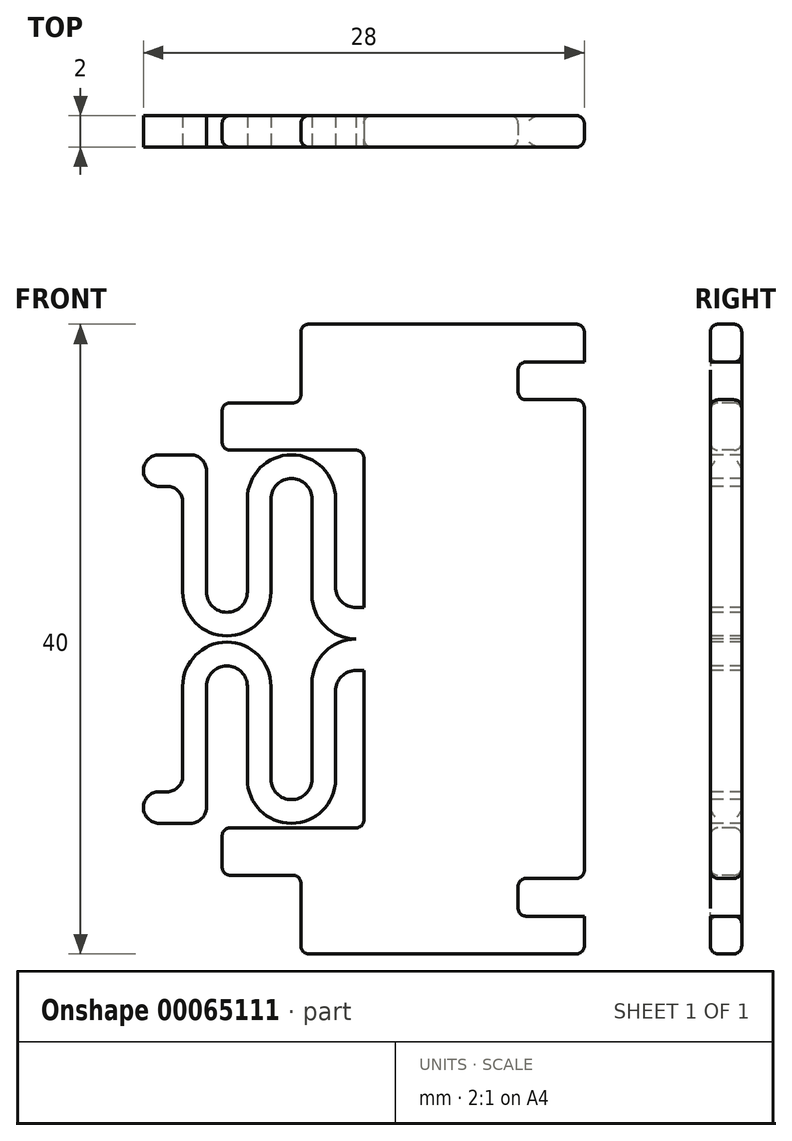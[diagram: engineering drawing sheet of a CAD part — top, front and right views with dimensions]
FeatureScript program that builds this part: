
annotation { "Feature Type Name" : "Feature", "Feature Type Description" : "" }
export const myFeature = defineFeature(function(context is Context, id is Id, definition is map)
    precondition{}
    {
        {
            var Q0;
            Q0=qCreatedBy(makeId("Top.planeOp"),FACE);
            var sketch = newSketch(context, id + "F0", { "sketchPlane" : qUnion([Q0])});
            skLineSegment(sketch, "E0.bottom", {"start": v(0, 0) * mm, "end": v(-18, 0) * mm});
            skLineSegment(sketch, "E0.top", {"start": v(0, 2) * mm, "end": v(-18, 2) * mm});
            skLineSegment(sketch, "E0.left", {"start": v(0, 0) * mm, "end": v(0, 2) * mm});
            skLineSegment(sketch, "E0.right", {"start": v(-18, 0) * mm, "end": v(-18, 2) * mm});
            skSolve(sketch);
        }
        {
            var Q0;
            Q0 = qSketchRegion(id + "F0", true);
            extrude(context, id + "F1", {"entities" : qUnion([Q0]), "depth" : 20 * mm});
        }
        {
            var Q0;
            Q0=qCreatedBy(makeId("Front.planeOp"),FACE);
            var sketch = newSketch(context, id + "F2", { "sketchPlane" : qUnion([Q0])});
            skLineSegment(sketch, "E1.bottom", {"start": v(-4.2, 17.6) * mm, "end": v(0, 17.6) * mm});
            skLineSegment(sketch, "E1.top", {"start": v(-4.2, 15.2) * mm, "end": v(0, 15.2) * mm});
            skLineSegment(sketch, "E1.left", {"start": v(-4.2, 17.6) * mm, "end": v(-4.2, 15.2) * mm});
            skLineSegment(sketch, "E1.right", {"start": v(0, 17.6) * mm, "end": v(0, 15.2) * mm});
            skSolve(sketch);
        }
        {
            var Q0;
            Q0 = qSketchRegion(id + "F2", true);
            extrude(context, id + "F3", {"entities" : qUnion([Q0]), "operationType" : NewBodyOperationType.REMOVE, "endBound" : BoundingType.THROUGH_ALL, "oppositeDirection" : true, "depth" : 25 * mm});
        }
        {
            var Q0;
            Q0=qCreatedBy(makeId("Front.planeOp"),FACE);
            var sketch = newSketch(context, id + "F4", { "sketchPlane" : qUnion([Q0])});
            skLineSegment(sketch, "E2.bottom", {"start": v(-14, 12) * mm, "end": v(-18, 12) * mm});
            skLineSegment(sketch, "E2.top", {"start": v(-14, 0) * mm, "end": v(-18, 0) * mm});
            skLineSegment(sketch, "E2.left", {"start": v(-14, 12) * mm, "end": v(-14, 0) * mm});
            skLineSegment(sketch, "E2.right", {"start": v(-18, 12) * mm, "end": v(-18, 0) * mm});
            skSolve(sketch);
        }
        {
            var Q0;
            Q0 = qSketchRegion(id + "F4", true);
            extrude(context, id + "F5", {"entities" : qUnion([Q0]), "operationType" : NewBodyOperationType.REMOVE, "endBound" : BoundingType.THROUGH_ALL, "oppositeDirection" : true, "depth" : 25 * mm});
        }
        {
            var Q0;
            Q0=qCreatedBy(makeId("Front.planeOp"),FACE);
            var sketch = newSketch(context, id + "F6", { "sketchPlane" : qUnion([Q0])});
            skLineSegment(sketch, "E3", {"start": v(-15.8, 11.7) * mm, "end": v(-21.4, 11.7) * mm, "construction": true});
            skLineSegment(sketch, "E4", {"start": v(-21.4, 11.7) * mm, "end": v(-21.4, 8.9) * mm, "construction": true});
            skLineSegment(sketch, "E5", {"start": v(-21.4, 1.7) * mm, "end": v(-24, 1.7) * mm, "construction": true});
            skLineSegment(sketch, "E6", {"start": v(-24, 1.7) * mm, "end": v(-24, 3) * mm, "construction": true});
            skLineSegment(sketch, "E7", {"start": v(-24, 11.7) * mm, "end": v(-28, 11.7) * mm});
            skLineSegment(sketch, "E8", {"start": v(-28, 11.7) * mm, "end": v(-28, 9.7) * mm});
            skLineSegment(sketch, "E9", {"start": v(-28, 9.7) * mm, "end": v(-25.5, 9.7) * mm});
            skLineSegment(sketch, "E10", {"start": v(-25.5, 9.7) * mm, "end": v(-25.5, 3) * mm});
            skLineSegment(sketch, "E11", {"start": v(-25.5, 0.2) * mm, "end": v(-19.9, 0.2) * mm, "construction": true});
            skLineSegment(sketch, "E12", {"start": v(-19.9, 0.2) * mm, "end": v(-19.9, 3) * mm, "construction": true});
            skLineSegment(sketch, "E13", {"start": v(-19.9, 10.2) * mm, "end": v(-17.3, 10.2) * mm, "construction": true});
            skLineSegment(sketch, "E14.bottom", {"start": v(-23, 15) * mm, "end": v(-18, 15) * mm});
            skLineSegment(sketch, "E14.top", {"start": v(-23, 12) * mm, "end": v(-18, 12) * mm});
            skLineSegment(sketch, "E14.left", {"start": v(-23, 15) * mm, "end": v(-23, 12) * mm});
            skLineSegment(sketch, "E14.right", {"start": v(-18, 15) * mm, "end": v(-18, 12) * mm});
            skArc(sketch, "E15", {"start": v(-24, 3) * mm, "mid": v(-22.7, 1.7) * mm, "end": v(-21.4, 3) * mm});
            skArc(sketch, "E16", {"start": v(-25.5, 3) * mm, "mid": v(-22.7, 0.2) * mm, "end": v(-19.9, 3) * mm});
            skLineSegment(sketch, "E17", {"start": v(-24, 3) * mm, "end": v(-24, 11.7) * mm});
            skLineSegment(sketch, "E18", {"start": v(-25.5, 3) * mm, "end": v(-25.5, 0.2) * mm, "construction": true});
            skLineSegment(sketch, "E19", {"start": v(-21.4, 3) * mm, "end": v(-21.4, 1.7) * mm, "construction": true});
            skLineSegment(sketch, "E20", {"start": v(-19.9, 3) * mm, "end": v(-19.9, 8.9) * mm});
            skArc(sketch, "E21", {"start": v(-15.8, 8.9) * mm, "mid": v(-18.6, 11.7) * mm, "end": v(-21.4, 8.9) * mm});
            skArc(sketch, "E22", {"start": v(-17.3, 8.9) * mm, "mid": v(-18.6, 10.2) * mm, "end": v(-19.9, 8.9) * mm});
            skLineSegment(sketch, "E23", {"start": v(-17.3, 10.2) * mm, "end": v(-17.3, 8.9) * mm, "construction": true});
            skLineSegment(sketch, "E24", {"start": v(-14.5, 0) * mm, "end": v(-14, 0) * mm});
            skLineSegment(sketch, "E25", {"start": v(-14, 0) * mm, "end": v(-14, 2) * mm});
            skLineSegment(sketch, "E26", {"start": v(-14, 2) * mm, "end": v(-14.5, 2) * mm});
            skLineSegment(sketch, "E27", {"start": v(-15.8, 3.3) * mm, "end": v(-15.8, 8.9) * mm});
            skLineSegment(sketch, "E28", {"start": v(-17.3, 8.9) * mm, "end": v(-17.3, 2.8) * mm});
            skLineSegment(sketch, "E29", {"start": v(-19.9, 8.9) * mm, "end": v(-19.9, 10.2) * mm, "construction": true});
            skLineSegment(sketch, "E30", {"start": v(-21.4, 8.9) * mm, "end": v(-21.4, 3) * mm});
            skLineSegment(sketch, "E31", {"start": v(-15.8, 8.9) * mm, "end": v(-15.8, 11.7) * mm, "construction": true});
            skPoint(sketch, "E32.visualSharp", {"position": v(-15.8, 2) * mm});
            skArc(sketch, "E32.filletArc", {"start": v(-15.8, 3.3) * mm, "mid": v(-15.42, 2.38) * mm, "end": v(-14.5, 2) * mm});
            skPoint(sketch, "E33.visualSharp", {"position": v(-17.3, 0) * mm});
            skArc(sketch, "E33.filletArc", {"start": v(-17.3, 2.8) * mm, "mid": v(-16.48, 0.82) * mm, "end": v(-14.5, 0) * mm});
            skSolve(sketch);
        }
        {
            var Q0;
            Q0 = qSketchRegion(id + "F6", true);
            extrude(context, id + "F7", {"entities" : qUnion([Q0]), "operationType" : NewBodyOperationType.ADD, "oppositeDirection" : true, "depth" : 2 * mm});
        }
        {
            var Q0;
            Q0=makeQuery(id+"F7.opExtrude","SWEPT_EDGE",EDGE,{"disambiguationData":[OSD([sQuery(id+"F6.wireOp",EDGE,"E6"),sQuery(id+"F6.wireOp",EDGE,"E7")])]});
            var Q1;
            Q1=makeQuery(id+"F7.opExtrude","SWEPT_EDGE",EDGE,{"disambiguationData":[OSD([sQuery(id+"F6.wireOp",EDGE,"E11"),sQuery(id+"F6.wireOp",EDGE,"E12")])]});
            var Q2;
            Q2=makeQuery(id+"F7.opExtrude","SWEPT_EDGE",EDGE,{"disambiguationData":[OSD([sQuery(id+"F6.wireOp",EDGE,"E10"),sQuery(id+"F6.wireOp",EDGE,"E11")])]});
            var Q3;
            Q3=makeQuery(id+"F7.opExtrude","SWEPT_EDGE",EDGE,{"disambiguationData":[OSD([sQuery(id+"F6.wireOp",EDGE,"E7"),sQuery(id+"F6.wireOp",EDGE,"E8")])]});
            var Q4;
            Q4=makeQuery(id+"F7.opExtrude","SWEPT_EDGE",EDGE,{"disambiguationData":[OSD([sQuery(id+"F6.wireOp",EDGE,"E8"),sQuery(id+"F6.wireOp",EDGE,"E9")])]});
            var Q5;
            Q5=makeQuery(id+"F7.opExtrude","SWEPT_EDGE",EDGE,{"disambiguationData":[OSD([sQuery(id+"F6.wireOp",EDGE,"E3"),sQuery(id+"F6.wireOp",EDGE,"E4")])]});
            var Q6;
            Q6=makeQuery(id+"F7.opExtrude","SWEPT_EDGE",EDGE,{"disambiguationData":[OSD([sQuery(id+"F6.wireOp",EDGE,"E25"),sQuery(id+"F6.wireOp",EDGE,"E26")])]});
            fillet(context, id + "F8", {"entities" : qUnion([Q0, Q1, Q2, Q3, Q4, Q5, Q6]), "radius" : 1 * mm, "tangentPropagation" : true, "allowEdgeOverflow" : false});
        }
        {
            var Q0;
            Q0=makeQuery(id+"F1.opExtrude","CAP_FACE",FACE,{"disambiguationData":[OSD([sQuery(id+"F0.wireOp",EDGE,"E0.bottom"),sQuery(id+"F0.wireOp",EDGE,"E0.top"),sQuery(id+"F0.wireOp",EDGE,"E0.left"),sQuery(id+"F0.wireOp",EDGE,"E0.right")])],"isStart":false});
            var Q1;
            {var subQ0=sQuery(id+"F0.wireOp",EDGE,"E0.bottom");var subQ1=sQuery(id+"F0.wireOp",EDGE,"E0.left");Q1=makeQuery(id+"F3.boolean.opBoolean","SPLIT",EDGE,{"disambiguationData":[TD([makeQuery(id+"F3.opExtrude","SWEPT_FACE",FACE,{"disambiguationData":[OSD([sQuery(id+"F2.wireOp",EDGE,"E1.bottom")])]})])],"derivedFrom":makeQuery(id+"F1.opExtrude","SWEPT_EDGE",EDGE,{"disambiguationData":[OSD([subQ0,subQ1])]})});}
            var Q2;
            {var subQ0=sQuery(id+"F0.wireOp",EDGE,"E0.bottom");var subQ1=sQuery(id+"F0.wireOp",EDGE,"E0.left");Q2=makeQuery(id+"F3.boolean.opBoolean","SPLIT",EDGE,{"disambiguationData":[TD([makeQuery(id+"F3.opExtrude","SWEPT_FACE",FACE,{"disambiguationData":[OSD([sQuery(id+"F2.wireOp",EDGE,"E1.top")])]})])],"derivedFrom":makeQuery(id+"F1.opExtrude","SWEPT_EDGE",EDGE,{"disambiguationData":[OSD([subQ0,subQ1])]})});}
            var Q3;
            {var subQ0=sQuery(id+"F0.wireOp",EDGE,"E0.left");var subQ1=sQuery(id+"F0.wireOp",EDGE,"E0.top");Q3=makeQuery(id+"F3.boolean.opBoolean","SPLIT",EDGE,{"disambiguationData":[TD([makeQuery(id+"F3.opExtrude","SWEPT_FACE",FACE,{"disambiguationData":[OSD([sQuery(id+"F2.wireOp",EDGE,"E1.top")])]})])],"derivedFrom":makeQuery(id+"F1.opExtrude","SWEPT_EDGE",EDGE,{"disambiguationData":[OSD([subQ1,subQ0])]})});}
            var Q4;
            {var subQ0=sQuery(id+"F0.wireOp",EDGE,"E0.left");var subQ1=sQuery(id+"F0.wireOp",EDGE,"E0.top");Q4=makeQuery(id+"F3.boolean.opBoolean","SPLIT",EDGE,{"disambiguationData":[TD([makeQuery(id+"F3.opExtrude","SWEPT_FACE",FACE,{"disambiguationData":[OSD([sQuery(id+"F2.wireOp",EDGE,"E1.bottom")])]})])],"derivedFrom":makeQuery(id+"F1.opExtrude","SWEPT_EDGE",EDGE,{"disambiguationData":[OSD([subQ1,subQ0])]})});}
            var Q5;
            Q5=makeQuery(id+"F3.boolean.opBoolean","COPY",EDGE,{"derivedFrom":makeQuery(id+"F3.opExtrude","SWEPT_EDGE",EDGE,{"disambiguationData":[OSD([sQuery(id+"F2.wireOp",EDGE,"E1.bottom"),sQuery(id+"F2.wireOp",EDGE,"E1.right")])]})});
            var Q6;
            Q6=makeQuery(id+"F3.boolean.opBoolean","COPY",FACE,{"derivedFrom":makeQuery(id+"F3.opExtrude","SWEPT_FACE",FACE,{"disambiguationData":[OSD([sQuery(id+"F2.wireOp",EDGE,"E1.left")])]})});
            var Q7;
            Q7=makeQuery(id+"F3.boolean.opBoolean","COPY",EDGE,{"derivedFrom":makeQuery(id+"F3.opExtrude","SWEPT_EDGE",EDGE,{"disambiguationData":[OSD([sQuery(id+"F2.wireOp",EDGE,"E1.bottom"),sQuery(id+"F2.wireOp",EDGE,"E1.left")])]})});
            var Q8;
            Q8=makeQuery(id+"F3.boolean.opBoolean","COPY",FACE,{"derivedFrom":makeQuery(id+"F3.opExtrude","SWEPT_FACE",FACE,{"disambiguationData":[OSD([sQuery(id+"F2.wireOp",EDGE,"E1.top")])]})});
            var Q9;
            Q9=makeQuery(id+"F7.opExtrude","SWEPT_FACE",FACE,{"disambiguationData":[OSD([sQuery(id+"F6.wireOp",EDGE,"E14.top")])]});
            var Q10;
            Q10=makeQuery(id+"F7.opExtrude","SWEPT_FACE",FACE,{"disambiguationData":[OSD([sQuery(id+"F6.wireOp",EDGE,"E14.left")])]});
            var Q11;
            {var subQ15=sQuery(id+"F6.wireOp",EDGE,"E14.bottom");var subQ17=sQuery(id+"F0.wireOp",EDGE,"E0.right");Q11=makeQuery(id+"F7.boolean.opBoolean","SPLIT",FACE,{"disambiguationData":[TD([makeQuery(id+"F7.opExtrude","SWEPT_FACE",FACE,{"disambiguationData":[OSD([subQ15])]})])],"derivedFrom":makeQuery(id+"F1.opExtrude","SWEPT_FACE",FACE,{"disambiguationData":[OSD([subQ17])]})});}
            var Q12;
            Q12=makeQuery(id+"F7.opExtrude","SWEPT_FACE",FACE,{"disambiguationData":[OSD([sQuery(id+"F6.wireOp",EDGE,"E14.bottom")])]});
            var Q13;
            {var subQ0=sQuery(id+"F6.wireOp",EDGE,"E13");var subQ1=sQuery(id+"F0.wireOp",EDGE,"E0.right");var subQ2=sQuery(id+"F0.wireOp",EDGE,"E0.bottom");Q13=makeQuery(id+"F7.boolean.opBoolean","SPLIT",EDGE,{"disambiguationData":[TD([makeQuery(id+"F7.opExtrude","SWEPT_FACE",FACE,{"disambiguationData":[OSD([subQ0])]})])],"derivedFrom":makeQuery(id+"F1.opExtrude","SWEPT_EDGE",EDGE,{"disambiguationData":[OSD([subQ2,subQ1])]})});}
            var Q14;
            {var subQ0=sQuery(id+"F0.wireOp",EDGE,"E0.right");var subQ1=sQuery(id+"F6.wireOp",EDGE,"E13");var subQ2=sQuery(id+"F0.wireOp",EDGE,"E0.top");Q14=makeQuery(id+"F7.boolean.opBoolean","SPLIT",EDGE,{"disambiguationData":[TD([makeQuery(id+"F7.opExtrude","SWEPT_FACE",FACE,{"disambiguationData":[OSD([subQ1])]})])],"derivedFrom":makeQuery(id+"F1.opExtrude","SWEPT_EDGE",EDGE,{"disambiguationData":[OSD([subQ2,subQ0])]})});}
            fillet(context, id + "F9", {"entities" : qUnion([Q0, Q1, Q2, Q3, Q4, Q5, Q6, Q7, Q8, Q9, Q10, Q11, Q12, Q13, Q14]), "radius" : .5 * mm, "tangentPropagation" : true, "allowEdgeOverflow" : false});
        }
        {
            var Q0;
            Q0=makeQuery(id+"F1.opExtrude","SWEPT_BODY",BODY,{"disambiguationData":[OSD([sQuery(id+"F0.wireOp",EDGE,"E0.bottom"),sQuery(id+"F0.wireOp",EDGE,"E0.top"),sQuery(id+"F0.wireOp",EDGE,"E0.left"),sQuery(id+"F0.wireOp",EDGE,"E0.right")])]});
            var Q1;
            Q1=qCreatedBy(makeId("Top.planeOp"),FACE);
            mirror(context, id + "F10", {"operationType" : NewBodyOperationType.ADD, "entities" : qUnion([Q0]), "mirrorPlane" : qUnion([Q1])});
        }
    });
